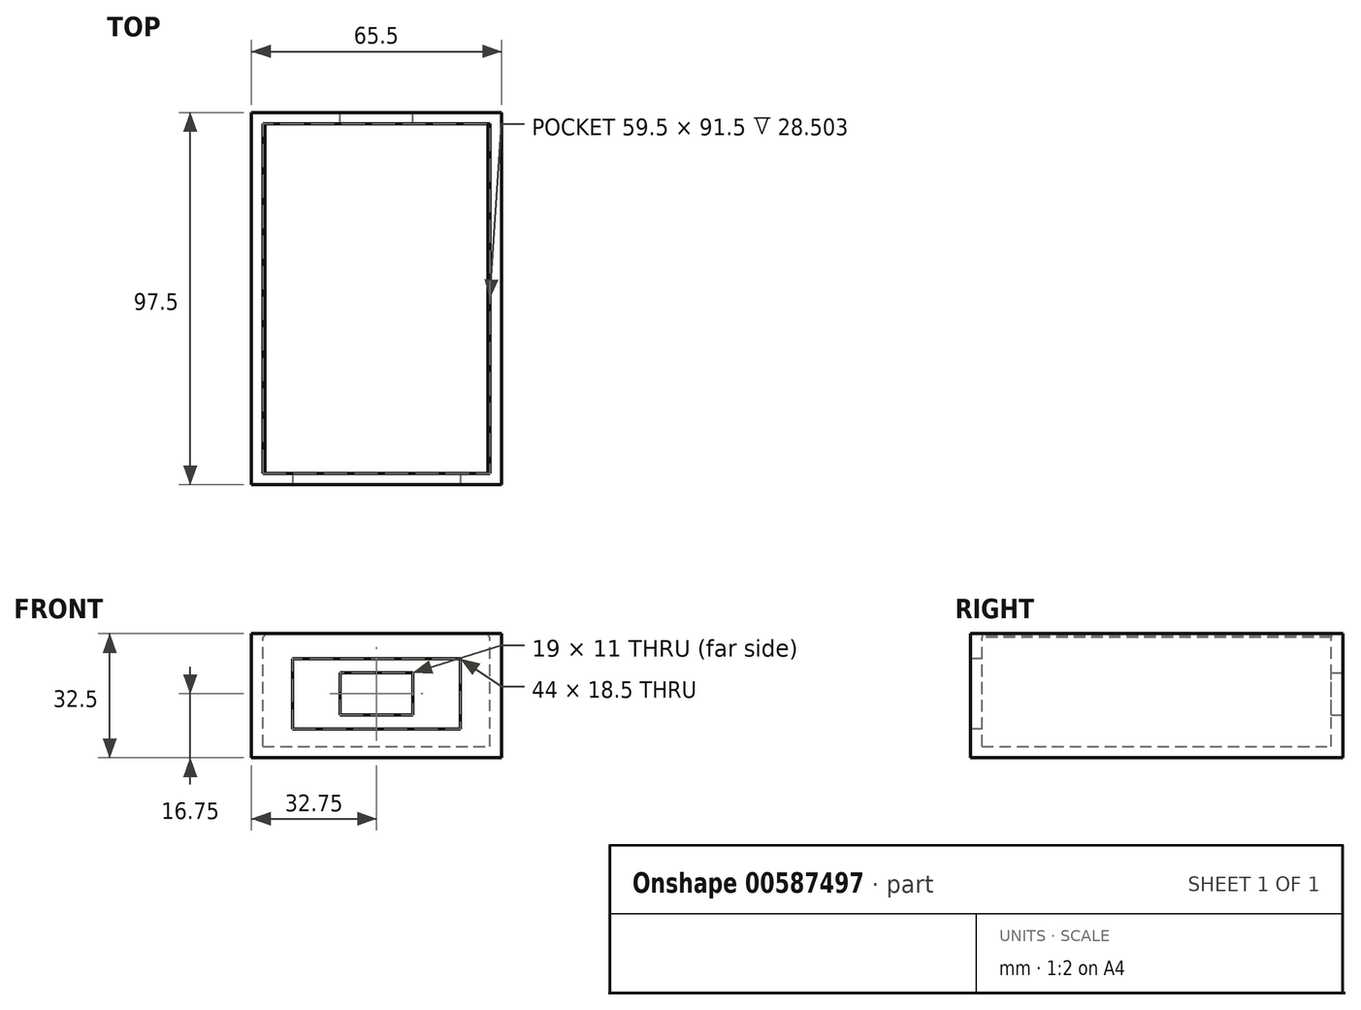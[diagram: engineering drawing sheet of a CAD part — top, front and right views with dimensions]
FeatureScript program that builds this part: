
annotation { "Feature Type Name" : "Feature", "Feature Type Description" : "" }
export const myFeature = defineFeature(function(context is Context, id is Id, definition is map)
    precondition{}
    {
        {
            var Q0;
            Q0=qCreatedBy(makeId("Top.planeOp"),FACE);
            var sketch = newSketch(context, id + "F0", { "sketchPlane" : qUnion([Q0])});
            skPoint(sketch, "E0.middle", {"position": v(0, 0) * mm});
            skLineSegment(sketch, "E1.bottom", {"start": v(-32.75, 48.75) * mm, "end": v(32.75, 48.75) * mm});
            skLineSegment(sketch, "E1.top", {"start": v(-32.75, -48.75) * mm, "end": v(32.75, -48.75) * mm});
            skLineSegment(sketch, "E1.left", {"start": v(-32.75, 48.75) * mm, "end": v(-32.75, -48.75) * mm});
            skLineSegment(sketch, "E1.right", {"start": v(32.75, 48.75) * mm, "end": v(32.75, -48.75) * mm});
            skSolve(sketch);
        }
        {
            var Q0;
            Q0 = qSketchRegion(id + "F0", true);
            extrude(context, id + "F1", {"entities" : qUnion([Q0]), "depth" : 32.5 * mm, "offsetDistance" : 25 * mm});
        }
        {
            var Q0;
            Q0=makeQuery(id+"F1.opExtrude","CAP_FACE",FACE,{"disambiguationData":[OSD([sQuery(id+"F0.wireOp",EDGE,"E1.bottom"),sQuery(id+"F0.wireOp",EDGE,"E1.top"),sQuery(id+"F0.wireOp",EDGE,"E1.left"),sQuery(id+"F0.wireOp",EDGE,"E1.right")])],"isStart":false});
            var sketch = newSketch(context, id + "F2", { "sketchPlane" : qUnion([Q0])});
            skLineSegment(sketch, "E2.bottom", {"start": v(-29.75, -45.75) * mm, "end": v(29.75, -45.75) * mm});
            skLineSegment(sketch, "E2.top", {"start": v(-29.75, 45.75) * mm, "end": v(29.75, 45.75) * mm});
            skLineSegment(sketch, "E2.left", {"start": v(-29.75, -45.75) * mm, "end": v(-29.75, 45.75) * mm});
            skLineSegment(sketch, "E2.right", {"start": v(29.75, -45.75) * mm, "end": v(29.75, 45.75) * mm});
            skPoint(sketch, "E2.middle", {"position": v(0, 0) * mm});
            skSolve(sketch);
        }
        {
            var Q0;
            Q0 = qSketchRegion(id + "F2", true);
            extrude(context, id + "F3", {"entities" : qUnion([Q0]), "operationType" : NewBodyOperationType.REMOVE, "oppositeDirection" : true, "depth" : 29.5 * mm, "offsetDistance" : 25 * mm});
        }
        {
            var Q0;
            Q0=makeQuery(id+"F1.opExtrude","SWEPT_FACE",FACE,{"disambiguationData":[OSD([sQuery(id+"F0.wireOp",EDGE,"E1.top")])]});
            var sketch = newSketch(context, id + "F4", { "sketchPlane" : qUnion([Q0])});
            skLineSegment(sketch, "E3", {"start": v(57.14, 16.75) * mm, "end": v(-56.8, 16.75) * mm, "construction": true});
            skLineSegment(sketch, "E4", {"start": v(0, 40.64) * mm, "end": v(0, -10.76) * mm, "construction": true});
            skLineSegment(sketch, "E5.bottom", {"start": v(-22, 7.5) * mm, "end": v(22, 7.5) * mm});
            skLineSegment(sketch, "E5.top", {"start": v(-22, 26) * mm, "end": v(22, 26) * mm});
            skLineSegment(sketch, "E5.left", {"start": v(-22, 7.5) * mm, "end": v(-22, 26) * mm});
            skLineSegment(sketch, "E5.right", {"start": v(22, 7.5) * mm, "end": v(22, 26) * mm});
            skPoint(sketch, "E5.middle", {"position": v(0, 16.75) * mm});
            skPoint(sketch, "E5.middle.positionSnap0", {"position": v(0, 14.94) * mm});
            skPoint(sketch, "E5.centerSnap0", {"position": v(0, 14.94) * mm});
            skSolve(sketch);
        }
        {
            var Q0;
            Q0 = qSketchRegion(id + "F4", true);
            extrude(context, id + "F5", {"entities" : qUnion([Q0]), "operationType" : NewBodyOperationType.REMOVE, "oppositeDirection" : true, "depth" : 3 * mm, "offsetDistance" : 25 * mm});
        }
        {
            var Q0;
            Q0=makeQuery(id+"F1.opExtrude","SWEPT_FACE",FACE,{"disambiguationData":[OSD([sQuery(id+"F0.wireOp",EDGE,"E1.bottom")])]});
            var sketch = newSketch(context, id + "F6", { "sketchPlane" : qUnion([Q0])});
            skLineSegment(sketch, "E6", {"start": v(0, 37.5) * mm, "end": v(0, -10.75) * mm, "construction": true});
            skPoint(sketch, "E6.endSnap0", {"position": v(0, 32.5) * mm});
            skLineSegment(sketch, "E7", {"start": v(-38.25, 16.75) * mm, "end": v(41.65, 16.75) * mm, "construction": true});
            skLineSegment(sketch, "E8", {"start": v(-40.1, 3) * mm, "end": v(47.56, 3) * mm, "construction": true});
            skLineSegment(sketch, "E9", {"start": v(-38.17, 11.25) * mm, "end": v(39.23, 11.25) * mm, "construction": true});
            skLineSegment(sketch, "E10", {"start": v(38.06, 22.25) * mm, "end": v(-38.06, 22.25) * mm, "construction": true});
            skLineSegment(sketch, "E11.bottom", {"start": v(-9.5, 11.25) * mm, "end": v(9.5, 11.25) * mm});
            skLineSegment(sketch, "E11.top", {"start": v(-9.5, 22.25) * mm, "end": v(9.5, 22.25) * mm});
            skLineSegment(sketch, "E11.left", {"start": v(-9.5, 11.25) * mm, "end": v(-9.5, 22.25) * mm});
            skLineSegment(sketch, "E11.right", {"start": v(9.5, 11.25) * mm, "end": v(9.5, 22.25) * mm});
            skPoint(sketch, "E11.middle", {"position": v(0, 16.75) * mm});
            skSolve(sketch);
        }
        {
            var Q0;
            Q0 = qSketchRegion(id + "F6", true);
            extrude(context, id + "F7", {"entities" : qUnion([Q0]), "operationType" : NewBodyOperationType.REMOVE, "oppositeDirection" : true, "depth" : 3 * mm, "offsetDistance" : 25 * mm});
        }
        {
            var Q0;
            Q0=makeQuery(id+"F1.opExtrude","SWEPT_FACE",FACE,{"disambiguationData":[OSD([sQuery(id+"F0.wireOp",EDGE,"E1.top")])]});
            var sketch = newSketch(context, id + "F8", { "sketchPlane" : qUnion([Q0])});
            skLineSegment(sketch, "E12", {"start": v(31.82, 32.5) * mm, "end": v(28.04, 32.5) * mm, "construction": true});
            skLineSegment(sketch, "E13", {"start": v(28.04, 32) * mm, "end": v(31.82, 32) * mm, "construction": true});
            skLineSegment(sketch, "E14", {"start": v(31.82, 31.5) * mm, "end": v(28.04, 31.5) * mm, "construction": true});
            skLineSegment(sketch, "E15", {"start": v(29.75, 32.5) * mm, "end": v(29.25, 32) * mm});
            skLineSegment(sketch, "E16", {"start": v(29.25, 32) * mm, "end": v(29.75, 31.5) * mm});
            skLineSegment(sketch, "E17", {"start": v(29.75, 32.5) * mm, "end": v(29.75, 31.5) * mm});
            skLineSegment(sketch, "E18.MirrorCS", {"start": v(-28.04, 32) * mm, "end": v(-31.82, 32) * mm, "construction": true});
            skLineSegment(sketch, "E19.MirrorCS", {"start": v(-31.82, 31.5) * mm, "end": v(-28.04, 31.5) * mm, "construction": true});
            skLineSegment(sketch, "E20.MirrorCS", {"start": v(-31.82, 32.5) * mm, "end": v(-28.04, 32.5) * mm, "construction": true});
            skLineSegment(sketch, "E21.MirrorCS", {"start": v(-29.75, 32.5) * mm, "end": v(-29.75, 31.5) * mm});
            skLineSegment(sketch, "E22.MirrorCS", {"start": v(-29.75, 32.5) * mm, "end": v(-29.25, 32) * mm});
            skLineSegment(sketch, "E23.MirrorCS", {"start": v(-29.25, 32) * mm, "end": v(-29.75, 31.5) * mm});
            skSolve(sketch);
        }
        {
            var Q0;
            Q0 = qSketchRegion(id + "F8", true);
            extrude(context, id + "F9", {"entities" : qUnion([Q0]), "operationType" : NewBodyOperationType.ADD, "oppositeDirection" : true, "depth" : 95 * mm, "offsetDistance" : 25 * mm});
        }
    });
